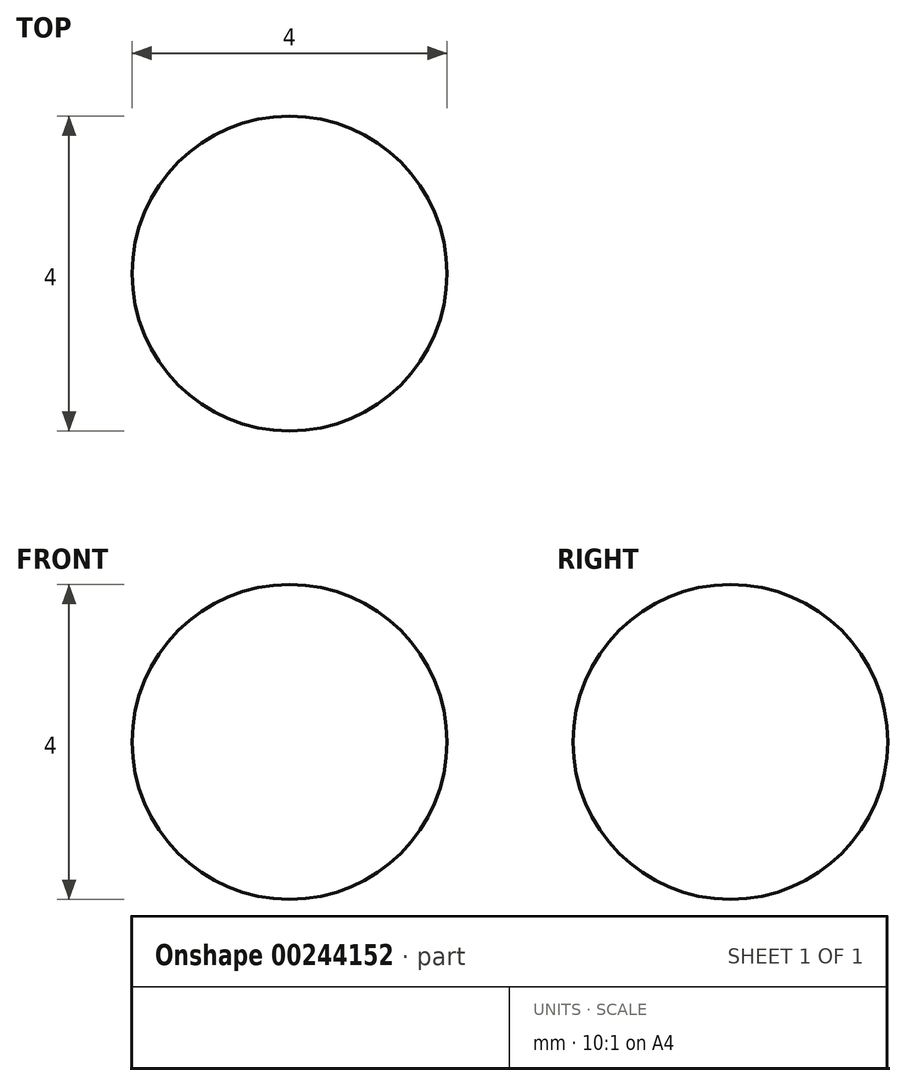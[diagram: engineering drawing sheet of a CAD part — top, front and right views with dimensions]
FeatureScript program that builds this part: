
annotation { "Feature Type Name" : "Feature", "Feature Type Description" : "" }
export const myFeature = defineFeature(function(context is Context, id is Id, definition is map)
    precondition{}
    {
        {
            var Q0;
            Q0=qCreatedBy(makeId("Front.planeOp"),FACE);
            var sketch = newSketch(context, id + "F0", { "sketchPlane" : qUnion([Q0])});
            skLineSegment(sketch, "E0", {"start": v(0, 0) * mm, "end": v(0, 4) * mm});
            skArc(sketch, "E1", {"start": v(0, 0) * mm, "mid": v(2, 2) * mm, "end": v(0, 4) * mm});
            skSolve(sketch);
        }
        {
            var Q0;
            Q0 = qSketchRegion(id + "F0", true);
            var Q1;
            Q1=sQuery(id+"F0.wireOp",EDGE,"E0");
            revolve(context, id + "F1", {"entities" : qUnion([Q0]), "axis" : qUnion([Q1]), "revolveType" : RevolveType.FULL});
        }
    });
